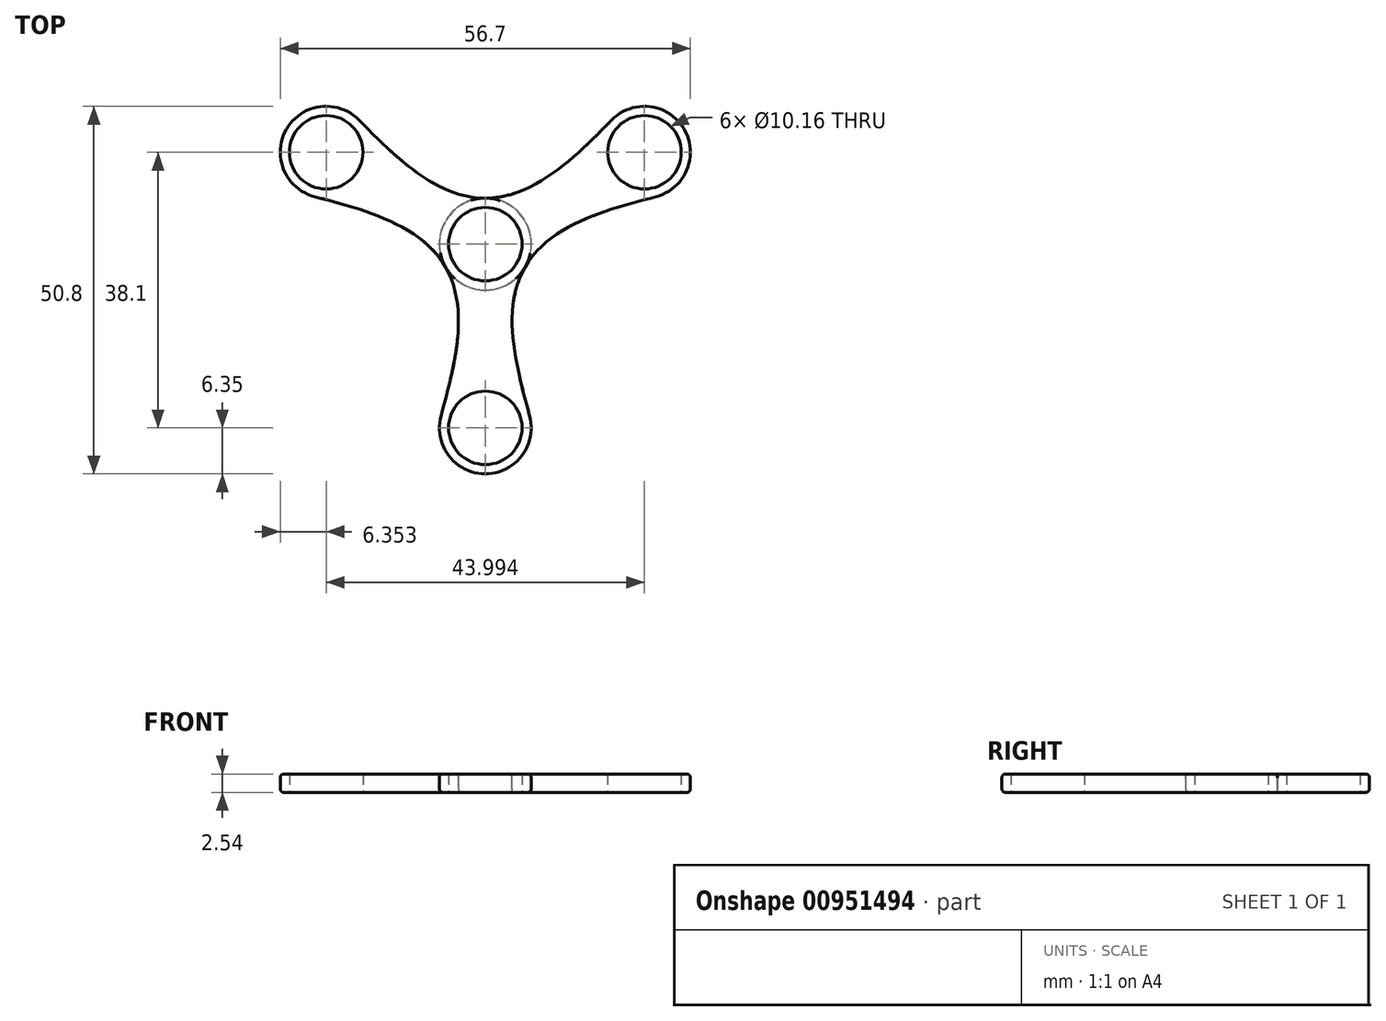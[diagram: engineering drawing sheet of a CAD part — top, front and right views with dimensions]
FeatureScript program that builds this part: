
annotation { "Feature Type Name" : "Feature", "Feature Type Description" : "" }
export const myFeature = defineFeature(function(context is Context, id is Id, definition is map)
    precondition{}
    {
        {
            var Q0;
            Q0=qCreatedBy(makeId("Top.planeOp"),FACE);
            var sketch = newSketch(context, id + "F0", { "sketchPlane" : qUnion([Q0])});
            skCircle(sketch, "E0", {"center": v(0, 0) * mm, "radius": 6.35 * mm});
            skCircle(sketch, "E1", {"center": v(0, -25.4) * mm, "radius": 6.35 * mm});
            skLineSegment(sketch, "E2", {"start": v(0, 0) * mm, "end": v(0, -25.4) * mm, "construction": true});
            skCircle(sketch, "E3", {"center": v(0, -25.4) * mm, "radius": 5.08 * mm});
            skCircle(sketch, "E4", {"center": v(0, 0) * mm, "radius": 5.08 * mm});
            skFitSpline(sketch, "E5", {"points": [v(-5.5, -3.18) * mm, v(-6.12, -23.72) * mm], "startDerivative": vector(10.14, -17.53) * mm, "endDerivative": vector(-5.65, -20.57) * mm});
            skFitSpline(sketch, "E6.MirrorCS", {"points": [v(5.5, -3.18) * mm, v(6.12, -23.72) * mm], "startDerivative": vector(-10.14, -17.53) * mm, "endDerivative": vector(5.65, -20.57) * mm});
            skLineSegment(sketch, "E7", {"start": v(0, 0) * mm, "end": v(10.44, -6.03) * mm, "construction": true});
            skSolve(sketch);
        }
        {
            var Q0;
            Q0 = qSketchRegion(id + "F0", true);
            extrude(context, id + "F1", {"entities" : qUnion([Q0]), "depth" : 2.54 * mm, "offsetDistance" : 25.4 * mm});
        }
        {
            var Q0;
            Q0=makeQuery(id+"F1.opExtrude","CAP_EDGE",EDGE,{"disambiguationData":[OSD([sQuery(id+"F0.wireOp",EDGE,"08f2d61a-6735-4184-b1bb-9d53bc714bfe0.MirrorCS")])],"isStart":false});
            var Q1;
            Q1=makeQuery(id+"F1.opExtrude","CAP_EDGE",EDGE,{"disambiguationData":[OSD([sQuery(id+"F0.wireOp",EDGE,"E0")])],"isStart":false});
            var Q2;
            Q2=makeQuery(id+"F1.opExtrude","CAP_EDGE",EDGE,{"disambiguationData":[OSD([sQuery(id+"F0.wireOp",EDGE,"E1")])],"isStart":false});
            var Q3;
            Q3=makeQuery(id+"F1.opExtrude","CAP_EDGE",EDGE,{"disambiguationData":[OSD([sQuery(id+"F0.wireOp",EDGE,"5119abf3-e59e-45a0-8de9-98e4e2e31942")])],"isStart":false});
            var Q4;
            Q4=makeQuery(id+"F1.opExtrude","CAP_EDGE",EDGE,{"disambiguationData":[OSD([sQuery(id+"F0.wireOp",EDGE,"E1")])],"isStart":true});
            var Q5;
            Q5=makeQuery(id+"F1.opExtrude","CAP_EDGE",EDGE,{"disambiguationData":[OSD([sQuery(id+"F0.wireOp",EDGE,"08f2d61a-6735-4184-b1bb-9d53bc714bfe0.MirrorCS")])],"isStart":true});
            var Q6;
            Q6=makeQuery(id+"F1.opExtrude","CAP_EDGE",EDGE,{"disambiguationData":[OSD([sQuery(id+"F0.wireOp",EDGE,"E0")])],"isStart":true});
            var Q7;
            Q7=makeQuery(id+"F1.opExtrude","CAP_EDGE",EDGE,{"disambiguationData":[OSD([sQuery(id+"F0.wireOp",EDGE,"5119abf3-e59e-45a0-8de9-98e4e2e31942")])],"isStart":true});
            fillet(context, id + "F2", {"entities" : qUnion([Q0, Q1, Q2, Q3, Q4, Q5, Q6, Q7]), "radius" : 0.5 * mm, "tangentPropagation" : true, "allowEdgeOverflow" : false});
        }
        {
            var Q0;
            Q0=qCreatedBy(makeId("Right.planeOp"),FACE);
            var sketch = newSketch(context, id + "F3", { "sketchPlane" : qUnion([Q0])});
            skLineSegment(sketch, "E8", {"start": v(0, 0) * mm, "end": v(0, 16.27) * mm});
            skSolve(sketch);
        }
        {
            var Q0;
            Q0=makeQuery(id+"F1.opExtrude","SWEPT_BODY",BODY,{"disambiguationData":[OSD([sQuery(id+"F0.wireOp",EDGE,"E0"),sQuery(id+"F0.wireOp",EDGE,"E1"),sQuery(id+"F0.wireOp",EDGE,"5119abf3-e59e-45a0-8de9-98e4e2e31942"),sQuery(id+"F0.wireOp",EDGE,"08f2d61a-6735-4184-b1bb-9d53bc714bfe0.MirrorCS"),sQuery(id+"F0.wireOp",EDGE,"E3"),sQuery(id+"F0.wireOp",EDGE,"E4")])]});
            var Q1;
            Q1=sQuery(id+"F3.wireOp",EDGE,"E8");
            circularPattern(context, id + "F4", {"entities" : qUnion([Q0]), "axis" : qUnion([Q1]), "angle" : 360 * degree, "instanceCount" : 3, "equalSpace" : true});
        }
    });
